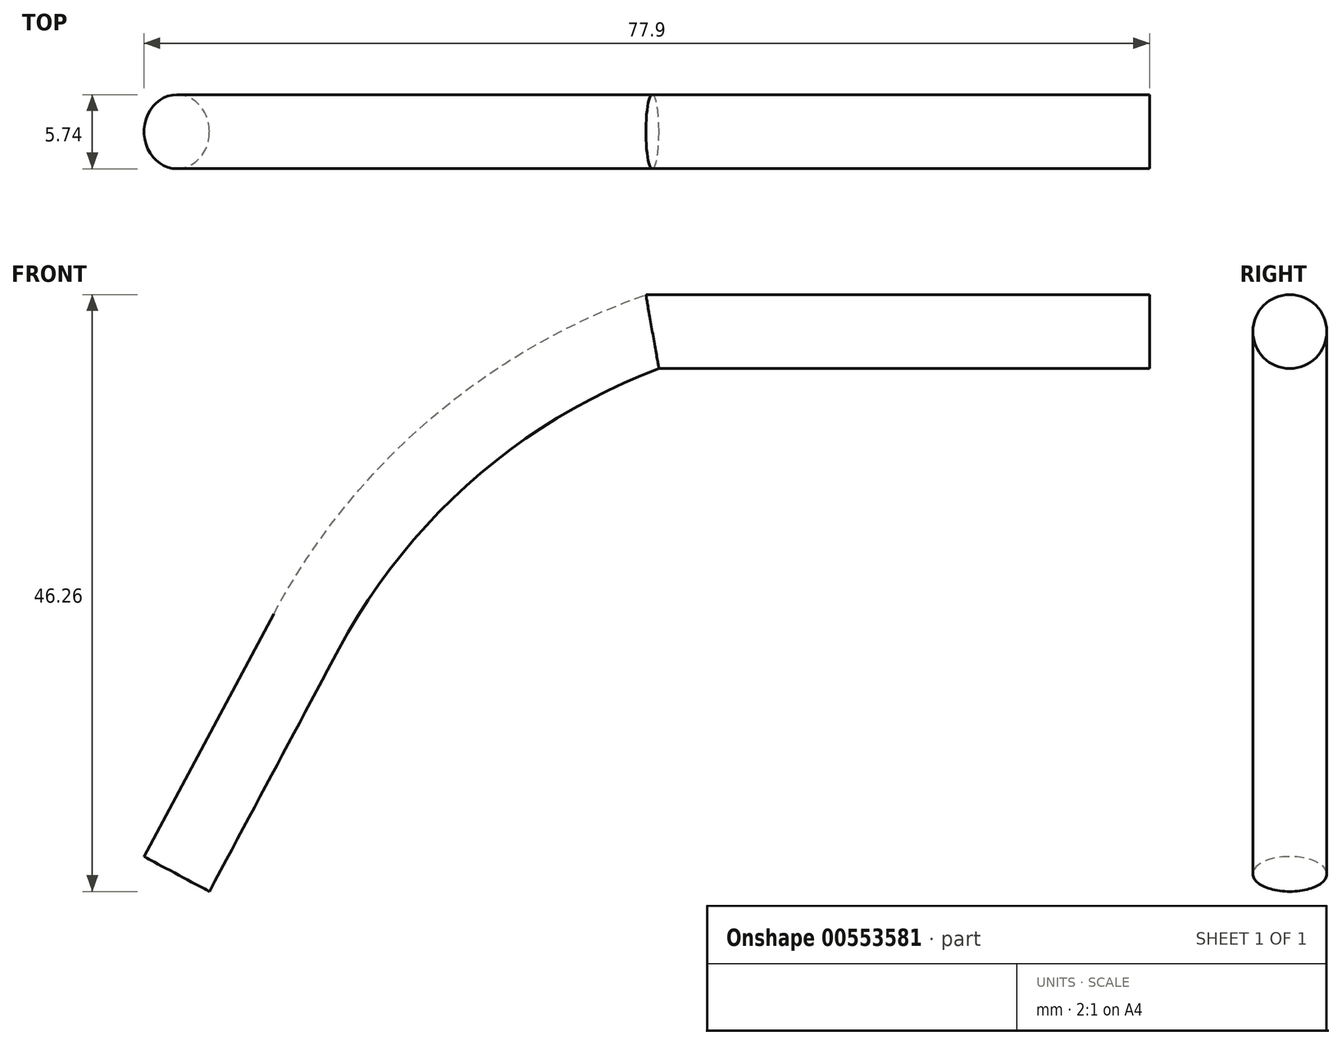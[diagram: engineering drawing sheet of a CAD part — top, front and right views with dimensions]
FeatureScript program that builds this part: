
annotation { "Feature Type Name" : "Feature", "Feature Type Description" : "" }
export const myFeature = defineFeature(function(context is Context, id is Id, definition is map)
    precondition{}
    {
        {
            var Q0;
            Q0=qCreatedBy(makeId("Front.planeOp"),FACE);
            var sketch = newSketch(context, id + "F0", { "sketchPlane" : qUnion([Q0])});
            skLineSegment(sketch, "E0", {"start": v(-46.44, 7.7) * mm, "end": v(-36.39, 26.51) * mm});
            skArc(sketch, "E1", {"start": v(-9.59, 49.74) * mm, "mid": v(-25.14, 40.6) * mm, "end": v(-36.39, 26.51) * mm});
            skLineSegment(sketch, "E2", {"start": v(-9.59, 49.74) * mm, "end": v(28.93, 49.74) * mm});
            skSolve(sketch);
        }
        {
            var Q0;
            Q0=sQuery(id+"F0.wireOp",EDGE,"E0");
            var Q1;
            Q1=sQuery(id+"F0.wireOp",VERTEX,"E0.start");
            cPlane(context, id + "F1", {"entities" : qUnion([Q0, Q1]), "cplaneType" : CPlaneType.LINE_POINT, "offset" : 25 * mm, "width" : 150 * mm, "height" : 150 * mm});
        }
        {
            var Q0;
            Q0=qCreatedBy(id+"F1.planeOp",FACE);
            var sketch = newSketch(context, id + "F2", { "sketchPlane" : qUnion([Q0])});
            skPoint(sketch, "E3.0", {"position": v(-44.59, 0) * mm});
            skCircle(sketch, "E4", {"center": v(-44.59, 0) * mm, "radius": 2.87 * mm});
            skSolve(sketch);
        }
        {
            var Q0;
            Q0=makeQuery(id+"F2.imprint","IMPRINT",FACE,{"disambiguationData":[TD([[makeQuery(id+"F2.imprint","IMPRINT",EDGE,{"derivedFrom":sQuery(id+"F2.wireOp",EDGE,"E4")}),1.0]])]});
            var Q1;
            Q1=sQuery(id+"F0.wireOp",EDGE,"E2");
            var Q2;
            Q2=sQuery(id+"F0.wireOp",EDGE,"E1");
            var Q3;
            Q3=sQuery(id+"F0.wireOp",EDGE,"E0");
            sweep(context, id + "F3", {"profiles" : qUnion([Q0]), "path" : qUnion([Q1, Q2, Q3])});
        }
    });
